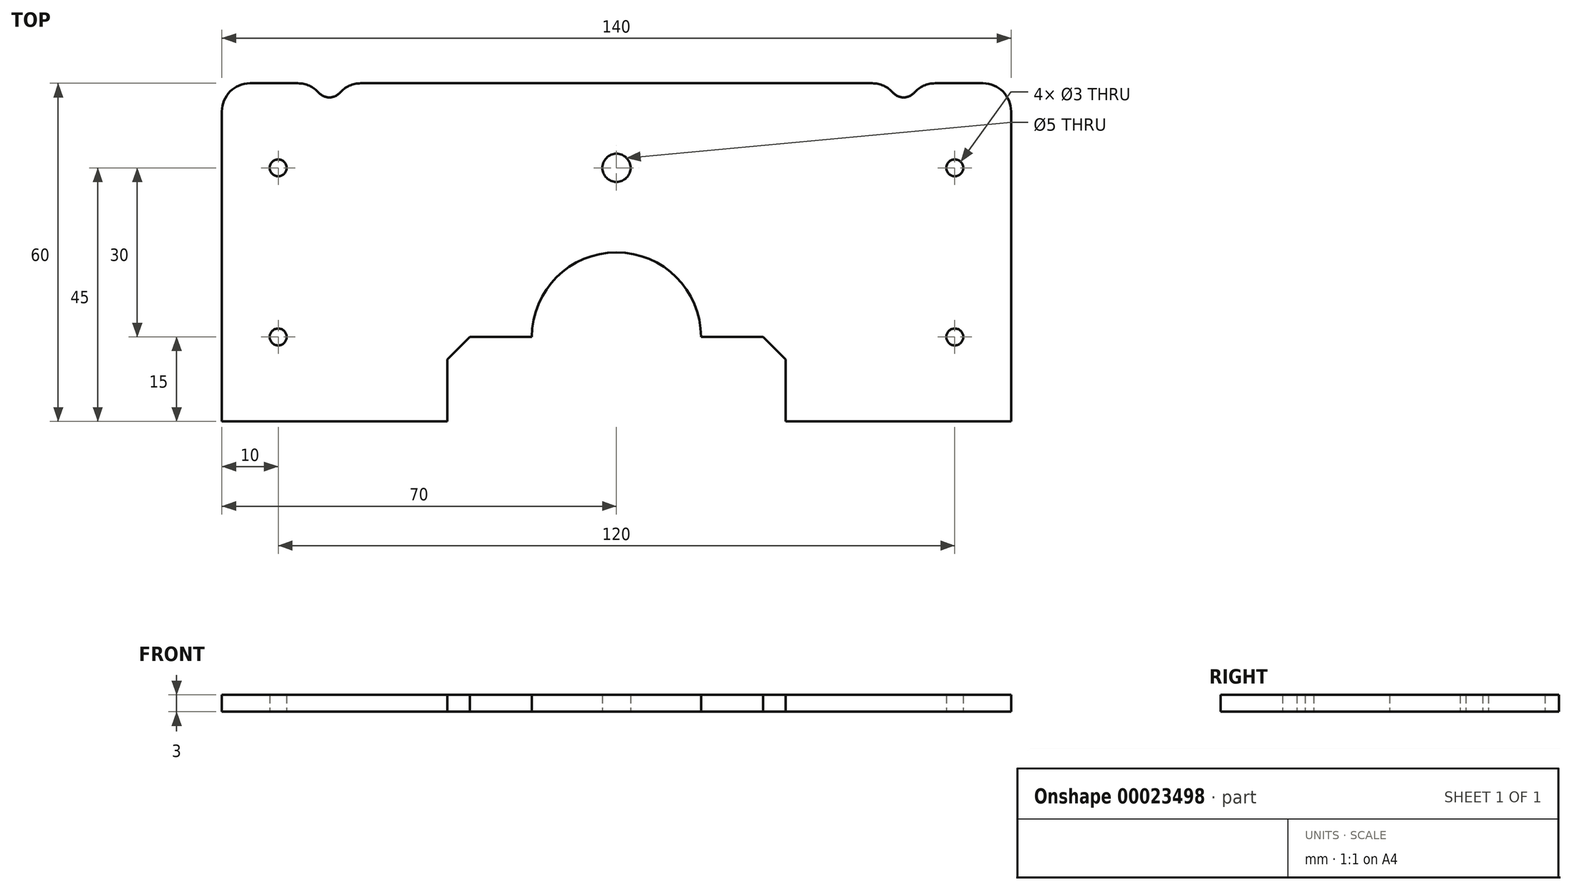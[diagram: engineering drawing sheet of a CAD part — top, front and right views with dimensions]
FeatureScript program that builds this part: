
annotation { "Feature Type Name" : "Feature", "Feature Type Description" : "" }
export const myFeature = defineFeature(function(context is Context, id is Id, definition is map)
    precondition{}
    {
        {
            var Q0;
            Q0=qCreatedBy(makeId("Top.planeOp"),FACE);
            var sketch = newSketch(context, id + "F0", { "sketchPlane" : qUnion([Q0])});
            skLineSegment(sketch, "E0.rect.bottom", {"start": v(70, 30) * mm, "end": v(53.43, 30) * mm});
            skLineSegment(sketch, "E0.rect.top", {"start": v(70, -30) * mm, "end": v(30, -30) * mm});
            skLineSegment(sketch, "E0.rect.left", {"start": v(70, 30) * mm, "end": v(70, -30) * mm});
            skLineSegment(sketch, "E0.rect.right", {"start": v(-70, 30) * mm, "end": v(-70, -30) * mm});
            skPoint(sketch, "E0.rect.middle", {"position": v(0, 0) * mm});
            skArc(sketch, "E1", {"start": v(15, -15) * mm, "mid": v(0, 0) * mm, "end": v(-15, -15) * mm});
            skLineSegment(sketch, "E2", {"start": v(-30, -15) * mm, "end": v(-15, -15) * mm});
            skLineSegment(sketch, "E3", {"start": v(30, -15) * mm, "end": v(30, -30) * mm});
            skLineSegment(sketch, "E4", {"start": v(-30, -15) * mm, "end": v(-30, -30) * mm});
            skPoint(sketch, "E5.orphan", {"position": v(-70, -15) * mm});
            skLineSegment(sketch, "E6.trimOffspring", {"start": v(-30, -30) * mm, "end": v(-70, -30) * mm});
            skLineSegment(sketch, "E7.trimOffspring", {"start": v(15, -15) * mm, "end": v(30, -15) * mm});
            skCircle(sketch, "E8", {"center": v(-60, -15) * mm, "radius": 1.5 * mm});
            skCircle(sketch, "E9", {"center": v(-60, 15) * mm, "radius": 1.5 * mm});
            skCircle(sketch, "E10.MirrorC", {"center": v(60, 15) * mm, "radius": 1.5 * mm});
            skCircle(sketch, "E11.MirrorC", {"center": v(60, -15) * mm, "radius": 1.5 * mm});
            skCircle(sketch, "E12", {"center": v(0, 15) * mm, "radius": 2.5 * mm});
            skArc(sketch, "E13", {"start": v(-53.43, 30) * mm, "mid": v(-50.93, 27.5) * mm, "end": v(-48.43, 30) * mm});
            skArc(sketch, "E14.MirrorC", {"start": v(53.43, 30) * mm, "mid": v(50.93, 27.5) * mm, "end": v(48.43, 30) * mm});
            skLineSegment(sketch, "E15.trimOffspring", {"start": v(-53.43, 30) * mm, "end": v(-70, 30) * mm});
            skLineSegment(sketch, "E16.trimOffspring", {"start": v(-29.24, 30) * mm, "end": v(-48.43, 30) * mm});
            skLineSegment(sketch, "E17.trimOffspring", {"start": v(24.24, 30) * mm, "end": v(-24.24, 30) * mm});
            skLineSegment(sketch, "E18.trimOffspring", {"start": v(48.43, 30) * mm, "end": v(29.24, 30) * mm});
            skLineSegment(sketch, "E19", {"start": v(-29.24, 30) * mm, "end": v(-24.24, 30) * mm});
            skLineSegment(sketch, "E20", {"start": v(24.24, 30) * mm, "end": v(29.24, 30) * mm});
            skSolve(sketch);
        }
        {
            var Q0;
            Q0 = qSketchRegion(id + "F0", true);
            extrude(context, id + "F1", {"entities" : qUnion([Q0]), "depth" : 3 * mm});
        }
        {
            var Q0;
            Q0 = qSketchRegion(id + "F0", true);
            extrude(context, id + "F2", {"entities" : qUnion([Q0]), "operationType" : NewBodyOperationType.ADD, "depth" : 3 * mm});
        }
        {
            var Q0;
            Q0=makeQuery(id+"F1.opExtrude","SWEPT_EDGE",EDGE,{"disambiguationData":[OSD([sQuery(id+"F0.wireOp",EDGE,"E2"),sQuery(id+"F0.wireOp",EDGE,"E4")])]});
            var Q1;
            Q1=makeQuery(id+"F1.opExtrude","SWEPT_EDGE",EDGE,{"disambiguationData":[OSD([sQuery(id+"F0.wireOp",EDGE,"E3"),sQuery(id+"F0.wireOp",EDGE,"E7.trimOffspring")])]});
            chamfer(context, id + "F3", {"entities" : qUnion([Q0, Q1]), "width" : 4 * mm, "tangentPropagation" : true});
        }
        {
            var Q0;
            Q0=makeQuery(id+"F1.opExtrude","SWEPT_EDGE",EDGE,{"disambiguationData":[OSD([sQuery(id+"F0.wireOp",EDGE,"E0.rect.right"),sQuery(id+"F0.wireOp",EDGE,"E15.trimOffspring")])]});
            var Q1;
            Q1=makeQuery(id+"F1.opExtrude","SWEPT_EDGE",EDGE,{"disambiguationData":[OSD([sQuery(id+"F0.wireOp",EDGE,"E0.rect.bottom"),sQuery(id+"F0.wireOp",EDGE,"E0.rect.left")])]});
            fillet(context, id + "F4", {"entities" : qUnion([Q0, Q1]), "radius" : 5 * mm, "tangentPropagation" : true, "allowEdgeOverflow" : false});
        }
        {
            var Q0;
            Q0=makeQuery(id+"F1.opExtrude","SWEPT_EDGE",EDGE,{"disambiguationData":[OSD([sQuery(id+"F0.wireOp",EDGE,"E13"),sQuery(id+"F0.wireOp",EDGE,"E15.trimOffspring")])]});
            var Q1;
            Q1=makeQuery(id+"F1.opExtrude","SWEPT_EDGE",EDGE,{"disambiguationData":[OSD([sQuery(id+"F0.wireOp",EDGE,"E13"),sQuery(id+"F0.wireOp",EDGE,"E16.trimOffspring")])]});
            var Q2;
            Q2=makeQuery(id+"F1.opExtrude","SWEPT_EDGE",EDGE,{"disambiguationData":[OSD([sQuery(id+"F0.wireOp",EDGE,"E14.MirrorC"),sQuery(id+"F0.wireOp",EDGE,"E18.trimOffspring")])]});
            var Q3;
            Q3=makeQuery(id+"F1.opExtrude","SWEPT_EDGE",EDGE,{"disambiguationData":[OSD([sQuery(id+"F0.wireOp",EDGE,"E0.rect.bottom"),sQuery(id+"F0.wireOp",EDGE,"E14.MirrorC")])]});
            fillet(context, id + "F5", {"entities" : qUnion([Q0, Q1, Q2, Q3]), "radius" : 5 * mm, "tangentPropagation" : true, "allowEdgeOverflow" : false});
        }
    });
